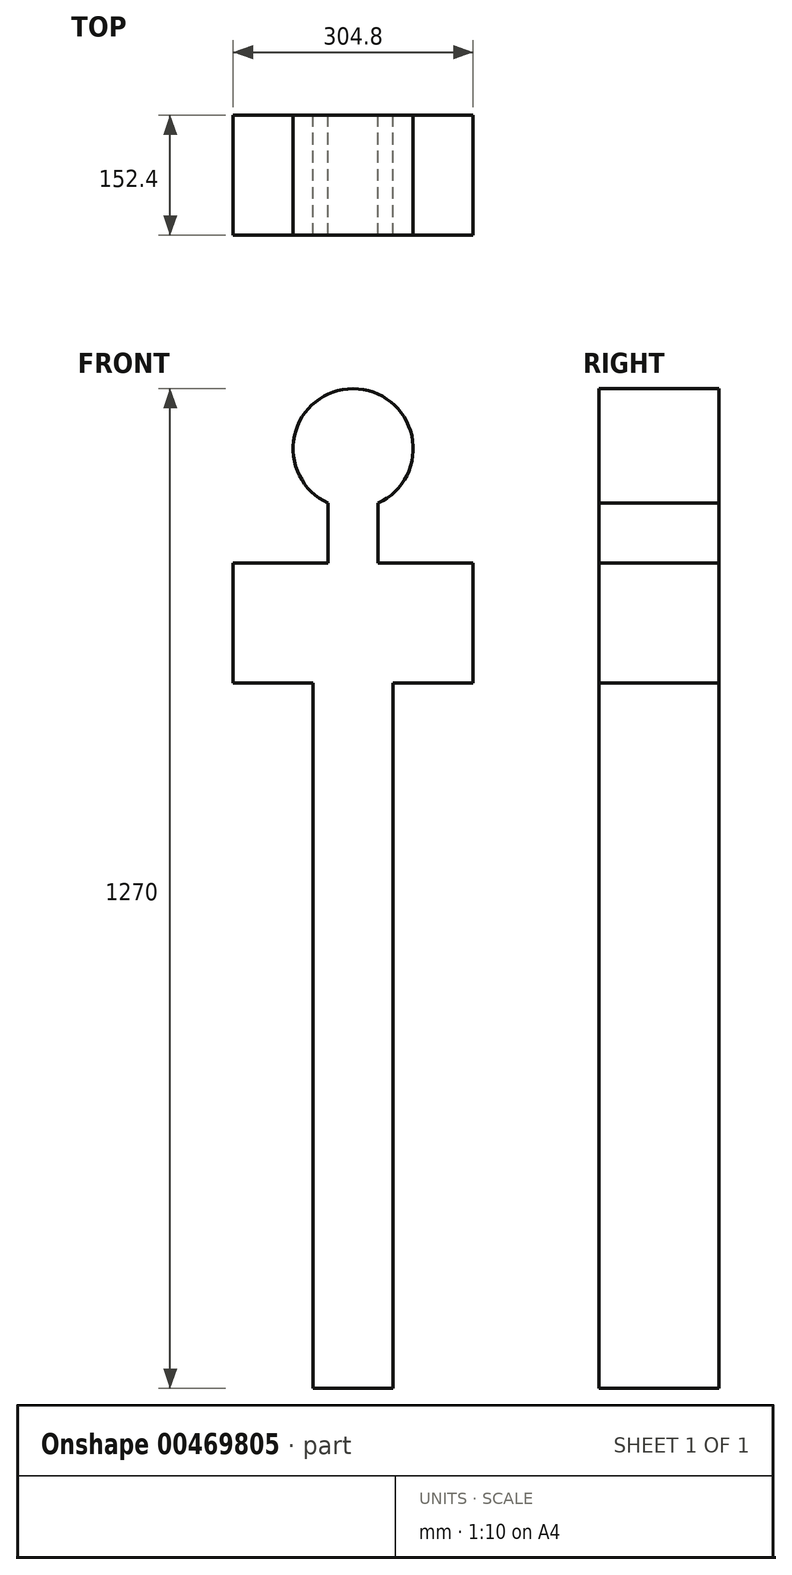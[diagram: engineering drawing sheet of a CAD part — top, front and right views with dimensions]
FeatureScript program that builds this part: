
annotation { "Feature Type Name" : "Feature", "Feature Type Description" : "" }
export const myFeature = defineFeature(function(context is Context, id is Id, definition is map)
    precondition{}
    {
        {
            var Q0;
            Q0=qCreatedBy(makeId("Front.planeOp"),FACE);
            var sketch = newSketch(context, id + "F0", { "sketchPlane" : qUnion([Q0])});
            skArc(sketch, "E0", {"start": v(31.75, -69.27) * mm, "mid": v(0, 76.2) * mm, "end": v(-31.75, -69.27) * mm});
            skLineSegment(sketch, "E1", {"start": v(-31.75, -145.62) * mm, "end": v(-152.4, -145.62) * mm});
            skLineSegment(sketch, "E2", {"start": v(-152.4, -145.62) * mm, "end": v(-152.4, -298.02) * mm});
            skLineSegment(sketch, "E3", {"start": v(-152.4, -298.02) * mm, "end": v(-50.8, -298.02) * mm});
            skLineSegment(sketch, "E4", {"start": v(-50.8, -298.02) * mm, "end": v(-50.8, -1193.8) * mm});
            skLineSegment(sketch, "E5", {"start": v(-50.8, -1193.8) * mm, "end": v(50.8, -1193.8) * mm});
            skLineSegment(sketch, "E6", {"start": v(50.8, -1193.8) * mm, "end": v(50.8, -298.02) * mm});
            skLineSegment(sketch, "E7", {"start": v(50.8, -298.02) * mm, "end": v(152.4, -298.02) * mm});
            skLineSegment(sketch, "E8", {"start": v(152.4, -298.02) * mm, "end": v(152.4, -145.62) * mm});
            skLineSegment(sketch, "E9", {"start": v(152.4, -145.62) * mm, "end": v(31.75, -145.62) * mm});
            skLineSegment(sketch, "E10", {"start": v(-31.75, -145.62) * mm, "end": v(-31.75, -69.27) * mm});
            skLineSegment(sketch, "E11", {"start": v(31.75, -145.62) * mm, "end": v(31.75, -69.27) * mm});
            skSolve(sketch);
        }
        {
            var Q0;
            Q0=qSketchRegion(id+"F0",true);
            extrude(context, id + "F1", {"entities" : qUnion([Q0]), "depth" : 152.4 * mm});
        }
    });
